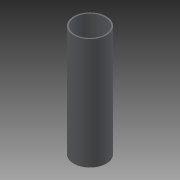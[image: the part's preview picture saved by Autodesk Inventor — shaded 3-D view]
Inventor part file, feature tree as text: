
AUTODESK INVENTOR PART (.ipt)
format: ipt  version: 2014 (Build 180170000, 170)  size: 102,400 bytes
history: native  units: in
note: dims shown in document units (in); Inventor stores cm internally (conversion verified against a paired STEP export)
features: other x14, revolve x1, sketch x1
ambient origin geometry x8: Origin, YZ Plane, XZ Plane, XY Plane, X Axis, Y Axis, Z Axis, Center Point
bodies: Solid1 (feature_tree)
feature tree (16):
  revolve  "Revolution1"  [1 undecoded]
  other  "tube_rear_XY"
  other  "tube_rear_YZ"
  other  "tube_rear_ZX"
  other  "tube_rear_X"
  other  "tube_rear_Y"
  other  "tube_rear_Z"
  other  "tube_rear_Center"
  other  "tube_rod_guide_XY"
  other  "tube_rod_guide_YZ"
  other  "tube_rod_guide_ZX"
  other  "tube_rod_guide_X"
  other  "tube_rod_guide_Y"
  other  "tube_rod_guide_Z"
  other  "tube_rod_guide_Center"
  sketch  "Sketch_4"  dims[d0=360.0deg]
note: 1 required parameter value undecoded (feature->parameter linkage not recoverable at this tier; creation-order binding heuristic only, values carry confidence <= 0.55)
